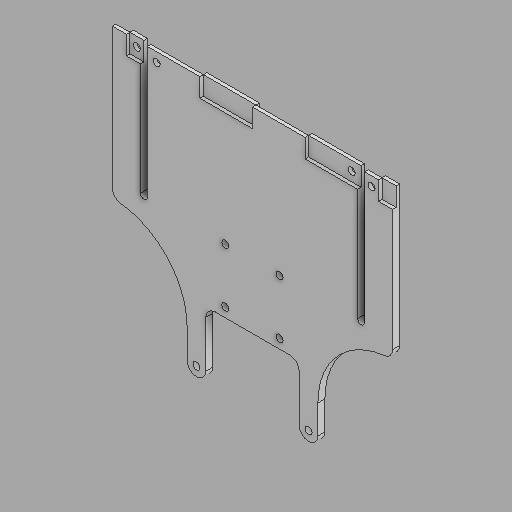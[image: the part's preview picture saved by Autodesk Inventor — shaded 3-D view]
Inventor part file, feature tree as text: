
AUTODESK INVENTOR PART (.ipt)
format: ipt  version: 2025.2 (Build 292293000, 293)  size: 273,408 bytes
history: native  units: in
note: dims shown in document units (in); Inventor stores cm internally (conversion verified against a paired STEP export)
features: sketch x7, extrude x5, hole x2, fillet x2
ambient origin geometry x8: Origin, YZ Plane, XZ Plane, XY Plane, X Axis, Y Axis, Z Axis, Center Point
bodies: Solid1 (feature_tree)
feature tree (16):
  extrude  "Extrusion1"  Depth=3.5in
  hole  "Hole1"  [1 undecoded]
  extrude  "Extrusion2"  Depth=0.1875in TaperAngle=0.0deg
  fillet  "Fillet1"  Radius=0.25in
  fillet  "Fillet2"  Radius=0.25in
  extrude  "Extrusion3"  Depth=1.4567in
  extrude  "Extrusion4"  Depth=6.0in
  extrude  "Extrusion5"  Depth=0.75in
  hole  "Hole2"  [1 undecoded]
  sketch  "Sketch1"  dims[d0=3.5in d1=13.0in]
  sketch  "Sketch2"  dims[d3=2.0in d4=0.5in]
  sketch  "Sketch3"  dims[d5=1.75in d6=0.1875in d7=0.0in d10=0.25in d11=0.25in]
  sketch  "Sketch4"  dims[d12=1.4567in d13=1.4567in]
  sketch  "Sketch5"  dims[d14=0.25in]
  sketch  "Sketch6"  dims[d15=0.1875in d16=0.75in d17=0.375in d18=0.25in d19=0.5635in d20=0.25in d21=0.0in d22=6.0in]
  sketch  "Sketch7"  dims[d23=0.1875in d24=0.75in d25=0.0in d26=0.0in d27=3.0in d28=0.25in d29=2.0in d30=0.5in d31=1.0in d32=0.0in d33=1.4062in d34=1.4062in d35=0.0938in d36=0.0in d37=0.0938in d38=0.0in d39=0.25in d40=0.25in d41=0.1875in d42=0.1875in d43=0.75in d44=0.375in d45=0.25in d46=0.5635in d47=1.0in d48=0.0in]
note: 2 required parameter values undecoded (feature->parameter linkage not recoverable at this tier; creation-order binding heuristic only, values carry confidence <= 0.55)
